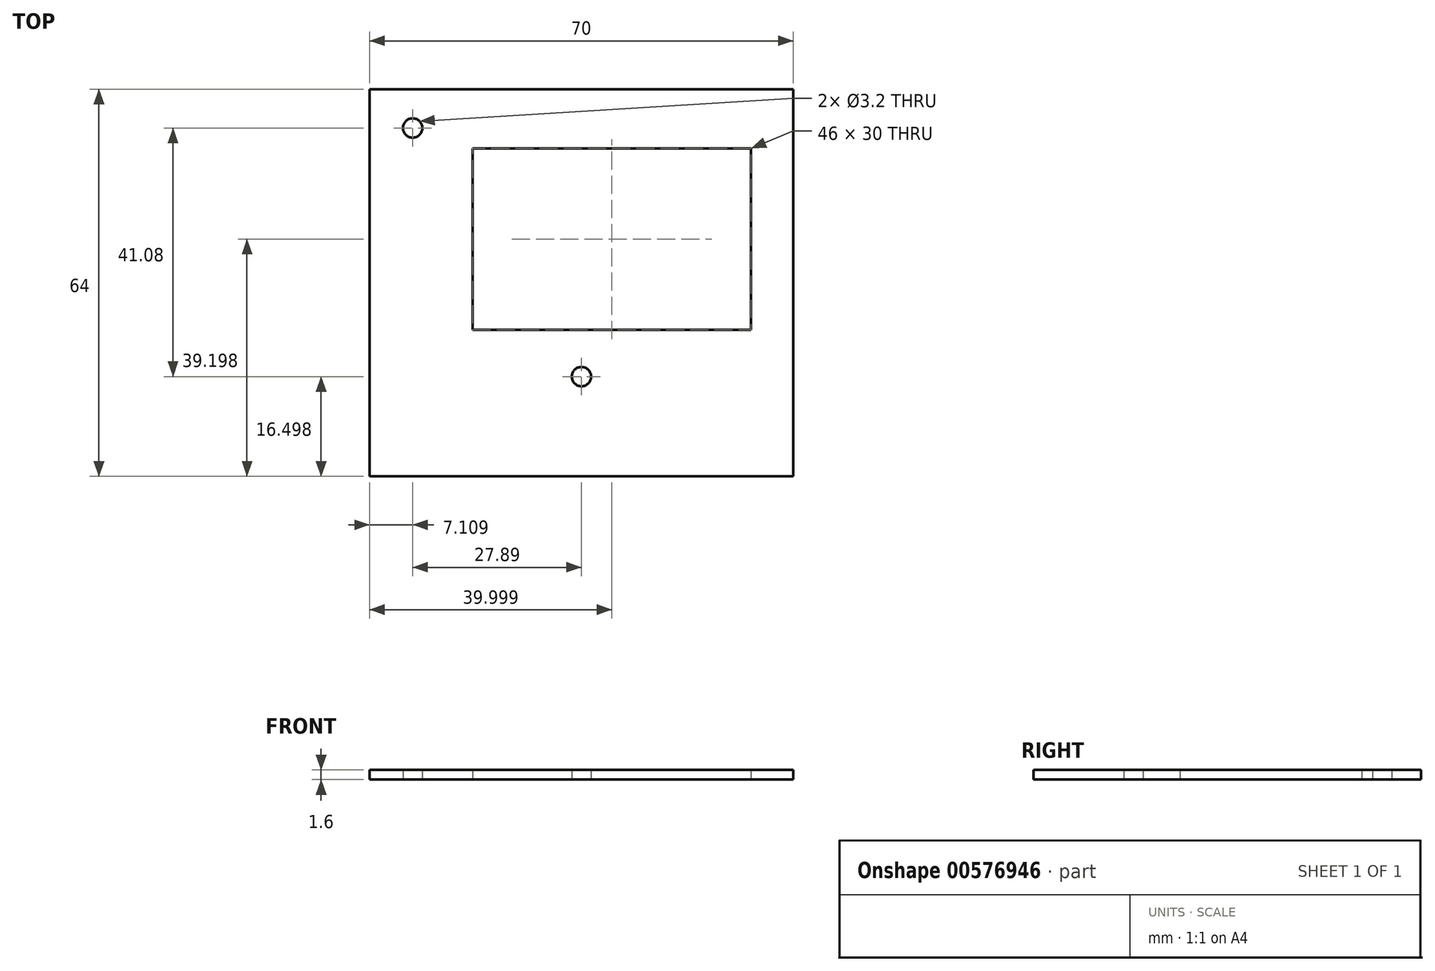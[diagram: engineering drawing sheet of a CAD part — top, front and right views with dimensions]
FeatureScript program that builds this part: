
annotation { "Feature Type Name" : "Feature", "Feature Type Description" : "" }
export const myFeature = defineFeature(function(context is Context, id is Id, definition is map)
    precondition{}
    {
        {
            var Q0;
            Q0=qCreatedBy(makeId("Top.planeOp"),FACE);
            var sketch = newSketch(context, id + "F0", { "sketchPlane" : qUnion([Q0])});
            skLineSegment(sketch, "E0.bottom", {"start": v(-28.51, 34.36) * mm, "end": v(41.49, 34.36) * mm});
            skLineSegment(sketch, "E0.top", {"start": v(-28.51, -29.64) * mm, "end": v(41.49, -29.64) * mm});
            skLineSegment(sketch, "E0.left", {"start": v(-28.51, 34.36) * mm, "end": v(-28.51, -29.64) * mm});
            skLineSegment(sketch, "E0.right", {"start": v(41.49, 34.36) * mm, "end": v(41.49, -29.64) * mm});
            skCircle(sketch, "E1", {"center": v(-21.4, 27.94) * mm, "radius": 1.6 * mm});
            skCircle(sketch, "E2", {"center": v(6.49, -13.14) * mm, "radius": 1.6 * mm});
            skLineSegment(sketch, "E3.bottom", {"start": v(-11.51, 24.56) * mm, "end": v(34.49, 24.56) * mm});
            skLineSegment(sketch, "E3.top", {"start": v(-11.51, -5.44) * mm, "end": v(34.49, -5.44) * mm});
            skLineSegment(sketch, "E3.left", {"start": v(-11.51, 24.56) * mm, "end": v(-11.51, -5.44) * mm});
            skLineSegment(sketch, "E3.right", {"start": v(34.49, 24.56) * mm, "end": v(34.49, -5.44) * mm});
            skLineSegment(sketch, "E4", {"start": v(34.49, 9.56) * mm, "end": v(41.49, 9.56) * mm, "construction": true});
            skLineSegment(sketch, "E5", {"start": v(14.32, 34.36) * mm, "end": v(14.32, 24.56) * mm, "construction": true});
            skLineSegment(sketch, "E6", {"start": v(-11.51, 12.16) * mm, "end": v(-28.51, 12.16) * mm, "construction": true});
            skLineSegment(sketch, "E7", {"start": v(-21.4, 27.94) * mm, "end": v(-28.51, 27.94) * mm, "construction": true});
            skLineSegment(sketch, "E8", {"start": v(-21.4, 27.94) * mm, "end": v(-21.4, 34.36) * mm, "construction": true});
            skLineSegment(sketch, "E9", {"start": v(6.49, -13.14) * mm, "end": v(6.49, -29.64) * mm, "construction": true});
            skLineSegment(sketch, "E10", {"start": v(6.49, -13.14) * mm, "end": v(-28.51, -13.14) * mm, "construction": true});
            skLineSegment(sketch, "E11.bottom", {"start": v(-28.51, -3.44) * mm, "end": v(-22.01, -3.44) * mm, "construction": true});
            skLineSegment(sketch, "E11.top", {"start": v(-28.51, -14.44) * mm, "end": v(-22.01, -14.44) * mm, "construction": true});
            skLineSegment(sketch, "E11.left", {"start": v(-28.51, -3.44) * mm, "end": v(-28.51, -14.44) * mm});
            skLineSegment(sketch, "E11.right", {"start": v(-22.01, -3.44) * mm, "end": v(-22.01, -14.44) * mm, "construction": true});
            skLineSegment(sketch, "E12", {"start": v(-25.26, -14.44) * mm, "end": v(-25.26, -29.64) * mm, "construction": true});
            skPoint(sketch, "E13", {"position": v(-26.51, 14.96) * mm});
            skLineSegment(sketch, "E14", {"start": v(-26.51, 14.96) * mm, "end": v(-28.51, 14.96) * mm, "construction": true});
            skLineSegment(sketch, "E15", {"start": v(-26.51, 14.96) * mm, "end": v(-26.51, 34.36) * mm, "construction": true});
            skSolve(sketch);
        }
        {
            var Q0;
            Q0 = qSketchRegion(id + "F0", true);
            extrude(context, id + "F1", {"entities" : qUnion([Q0]), "depth" : 1.6 * mm, "offsetDistance" : 25 * mm});
        }
    });
